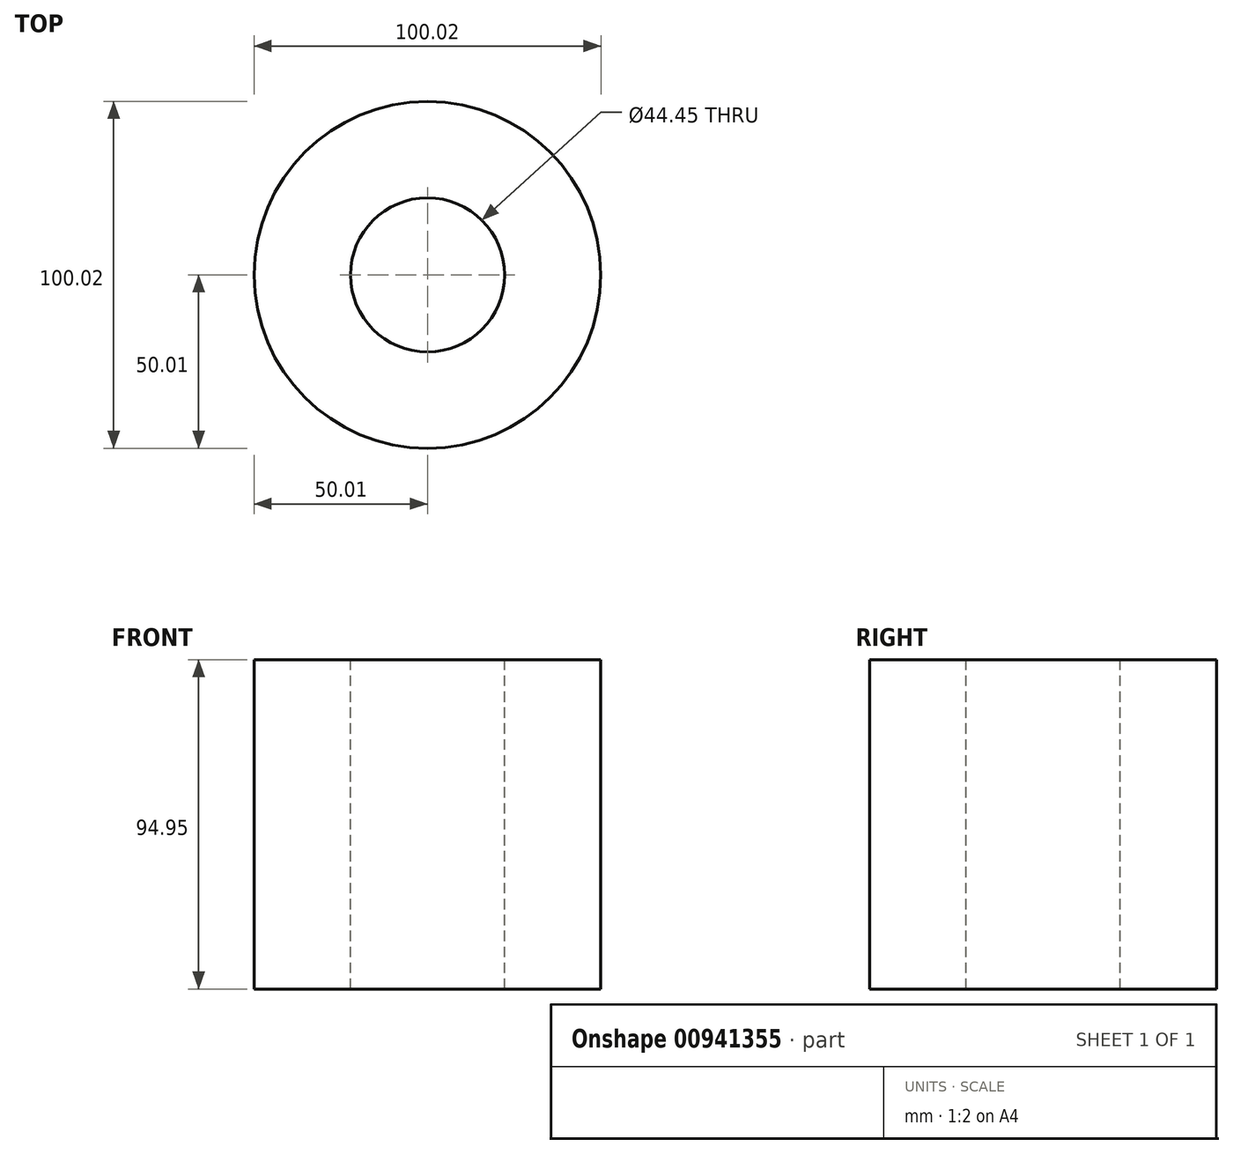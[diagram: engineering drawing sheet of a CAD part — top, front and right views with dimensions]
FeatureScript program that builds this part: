
annotation { "Feature Type Name" : "Feature", "Feature Type Description" : "" }
export const myFeature = defineFeature(function(context is Context, id is Id, definition is map)
    precondition{}
    {
        {
            var Q0;
            Q0=qCreatedBy(makeId("Top.planeOp"),FACE);
            var sketch = newSketch(context, id + "F0", { "sketchPlane" : qUnion([Q0])});
            skCircle(sketch, "E0", {"center": v(0, 0) * mm, "radius": 50 * mm});
            skSolve(sketch);
        }
        {
            var Q0;
            Q0=qSketchRegion(id+"F0",true);
            extrude(context, id + "F1", {"entities" : qUnion([Q0]), "depth" : 94.95 * mm, "offsetDistance" : 25.4 * mm});
        }
        {
            var Q0;
            Q0=makeQuery(id+"F1.opExtrude","CAP_FACE",FACE,{"disambiguationData":[OSD([sQuery(id+"F0.wireOp",EDGE,"E0")])],"isStart":false});
            var sketch = newSketch(context, id + "F2", { "sketchPlane" : qUnion([Q0])});
            skCircle(sketch, "E1", {"center": v(0, 0) * mm, "radius": 22.23 * mm});
            skSolve(sketch);
        }
        {
            var Q0;
            Q0=makeQuery(id+"F2.imprint","IMPRINT",FACE,{"disambiguationData":[TD([[makeQuery(id+"F2.imprint","IMPRINT",EDGE,{"derivedFrom":sQuery(id+"F2.wireOp",EDGE,"E1")}),1.0]])]});
            extrude(context, id + "F3", {"entities" : qUnion([Q0]), "operationType" : NewBodyOperationType.REMOVE, "endBound" : BoundingType.THROUGH_ALL, "oppositeDirection" : true, "depth" : 25.4 * mm, "offsetDistance" : 25.4 * mm});
        }
        {
            var Q0;
            Q0=makeQuery(id+"F1.opExtrude","CAP_FACE",FACE,{"disambiguationData":[OSD([sQuery(id+"F0.wireOp",EDGE,"E0")])],"isStart":false});
            var sketch = newSketch(context, id + "F4", { "sketchPlane" : qUnion([Q0])});
            skSolve(sketch);
        }
    });
